# Revit family: PRESTO 55 EMBUTIDO (C)
name_source: partatom
category: Aparatos sanitarios
revit_build: Autodesk Revit 2015 (Build: 20140223_1515(x64)
units: mm (PartAtom-declared; Revit-internal decimal feet)

## types (1)
- 55040
    Accionamiento = Por pulsador
    CAUDAL = 15 L/Min
    CIERRE = Automático en 30 seg.
    Comentarios de tipo = Cabeza intercambiable que comprende todo el mecanismo. Cuerpo, embellecedor y pulsador de latón cromado , piezas interioes en materiales resistentes a la corrosión y a las incrustaciones calcáreas.
    Conexión AC = Sí
    Conexión AF = Sí
    Código de montaje = C1030220
    Descripción = Grifo temporizado de un agua para instalación encastrada con cuerpo de latón y embellecedor cromado.
    Elevación por defecto = 1219 mm
    Fabricante = PRESTO IBÉRICA
    Imagen de tipo = <Ninguno>
    Material = LATON CROMADO
    Modelo = PRESTO 55 EMBUTIDO
    PESO BRUTO = 0.630 Kg
    REFERENCIA = 55040
    TIPO DE AGUA = Caliente
    Teléfono = (+34) 915 782 575
    URL = http://www.prestoiberica.com
